# Revit family: Loudspeaker_Bose_ArenaMatch-AMU208_with-Pan-and-Tilt-Bracket_1
name_source: partatom
category: Communication Devices
revit_build: Autodesk Revit 2015 (Build: 20160512_0715(x64)
units: mm (PartAtom-declared; Revit-internal decimal feet)

## types (2) — shared parameters
Crossover = Passive; separate bandpass filters per transducer (200 Hz and 1.2 kHz)
Default Elevation = 4' - 0"
Depth = 0' - 11"
Description = Bose Professional ArenaMatch loudspeakers bring proven DeltaQ sound quality and flexibility to outdoor installations — sports stadiums, arenas, outdoor entertainment centers, and more.
Edition number = 1
Enviromental = IEC 60529 IP55 for outdoor, direct-exposure installations
Frequency Range = 70 Hz to 18 kHz
Frequency Response = 80 Hz to 16 kHz
HF Driver = 1 x Bose EMB2S extended high-frequency compression driver (2-inch voice coil)
Height = 0' - 9 39/128"
LF Driver = 2 x Bose LF8 high-excursion 8-inch woofers (2-inch voice coil)
Manufacturer = Bose Professional
Mounting/Suspension = 2x M8 threaded inserts for U-bracket; 4x M8 threaded inserts on rear (127 × 70 mm, 4-bolt pattern)
Nominal Coverage Pattern = 90° × 60°
Nominal Impedance = 8 Ω
Nominal Sensitivity = Bose Extended Lifecycle Test: Free field - 95 dB, Wall/Ceilling - 97 dB; AES Transducer Test: Free field - 95 dB, Wall/Ceilling - 97 dB;
Power Connector = 1x barrier strip, (accepts 10 to 18 wire gauge)
Power Handling(Long-term continuous) = Bose Extended Lifecycle Test: 300W; AES Transducer Test: 400W
Power Handling(peak) = Bose Extended Lifecycle Test: 1200W; AES Transducer Test: 1600W
Product Guid = 99fa5c28-36be-4eb1-88a2-9f36c90cbf32
Product data url = https://bimobject.com
Rated Maximum SPL = Calculated max. SPL @ 1 m (Bose power test) -  Free field: 120 dB, Wall/Ceilling: 122 dB ; Calculated max. SPL @ 1 m (2-hour power test) - Free field: 121 dB, Wall/Ceilling: 123 dB; Calculated max. SPL @ 1 m (Bose power test), peak - Free field: 126 dB, Wall/Ceilling: 128 dB; Calculated max. SPL @ 1 m (2-hour power test),
peak -Free field: 127 dB, Wall/Ceilling: 129 dB;
Recommended High-pass Filter = 70 Hz with minimum 12-dB / octave filter
Transformer Taps Information = 70V: 5, 10, 20, 40, 80 W; 100V: 10, 20, 40, 80 W
URL = https://pro.bose.com
Weight = 17.01 kg
Width = 2' - 3"

## per-type parameters (varying)
| type | Bracket Material | Grill Material | Product code | Speaker Material |
| 811433-0110 Black | Metal-Bose-Black | Grill-Bose-Black | 811436-0110 | Matt-Bose-Black |
| 811433-0210 White | Metal-Bose-White | Grill-Bose-White | 811436-0210 | Matt-Bose-White |

note: column(s) folded — value = type name in every type: Model

## geometry (parser evidence)
native form markers: Blend x4, Sweep x10
no freeform markers — native parametric forms only
